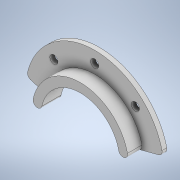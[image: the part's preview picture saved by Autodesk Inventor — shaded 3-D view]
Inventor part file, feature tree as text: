
AUTODESK INVENTOR PART (.ipt)
format: ipt  version: 2020 (Build 240168000, 168)  size: 149,504 bytes
history: native  units: in
note: dims shown in document units (in); Inventor stores cm internally (conversion verified against a paired STEP export)
features: extrude x3, sketch x3
ambient origin geometry x8: Origin, YZ Plane, XZ Plane, XY Plane, X Axis, Y Axis, Z Axis, Center Point
bodies: Solid1 (feature_tree)
feature tree (6):
  extrude  "Extrusion1"  Depth=1.0257in
  extrude  "Extrusion2"  Depth=0.5in TaperAngle=0.0deg
  extrude  "Extrusion3"  Depth=1.8in
  sketch  "Sketch1"  dims[d0=0.1165in d1=1.0257in]
  sketch  "Sketch2"  dims[d2=0.25in d3=0.5in d4=0.0in]
  sketch  "Sketch3"  dims[d5=1.2588in d6=1.8in d7=0.125in d8=0.0in d9=0.21in d10=1.5in d11=45.0deg d12=1.1811in d14=90.0deg d16=0.0in d17=0.0in]
